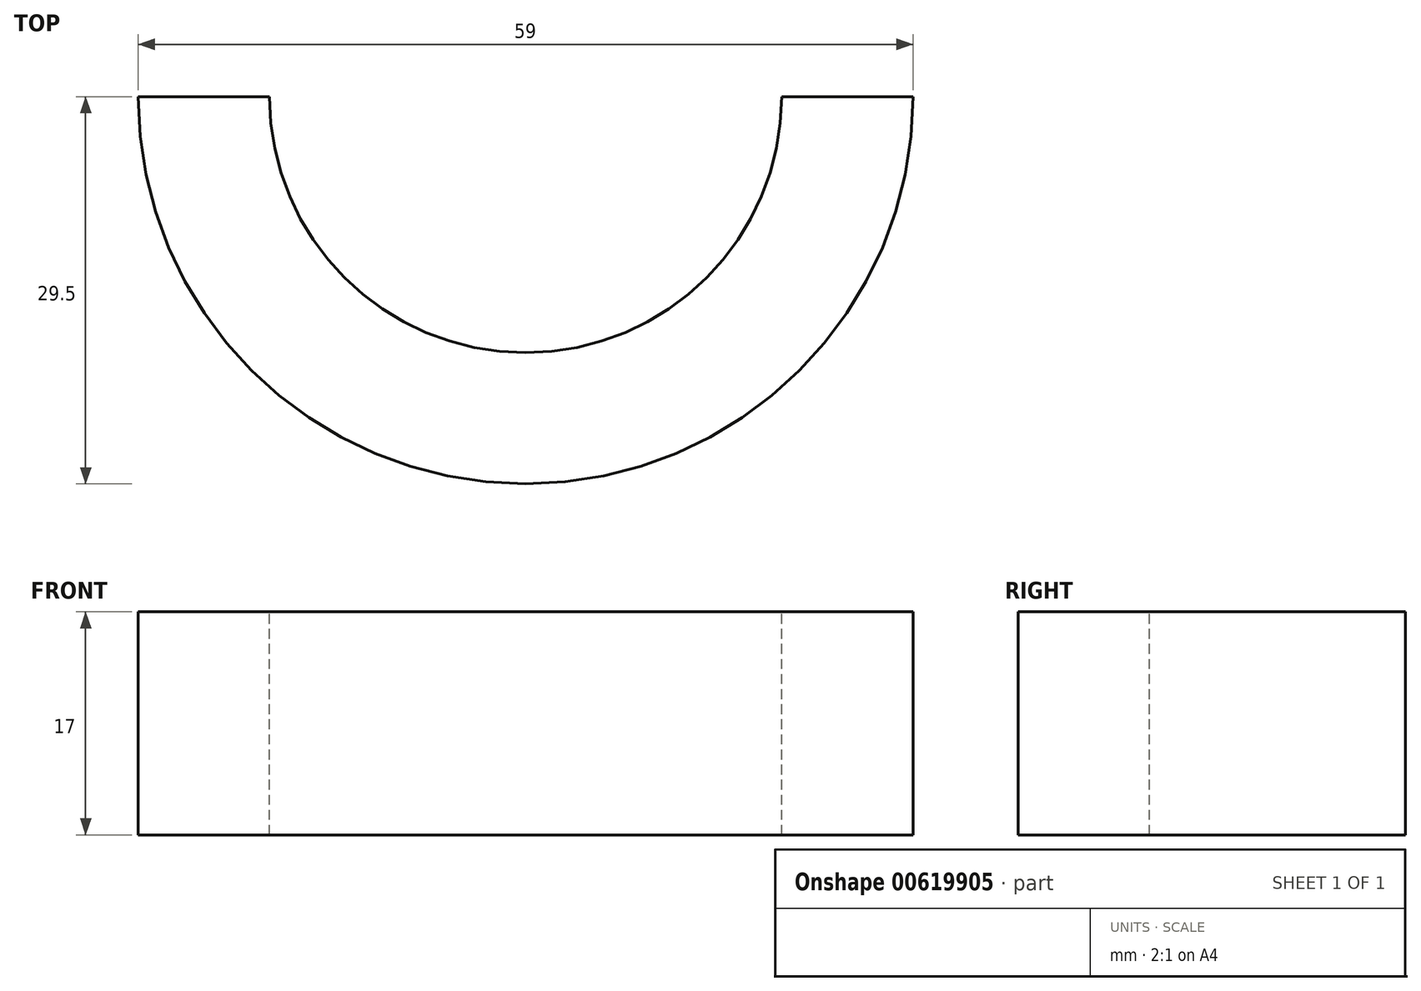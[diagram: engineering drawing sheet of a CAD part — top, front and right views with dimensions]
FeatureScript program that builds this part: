
annotation { "Feature Type Name" : "Feature", "Feature Type Description" : "" }
export const myFeature = defineFeature(function(context is Context, id is Id, definition is map)
    precondition{}
    {
        {
            var Q0;
            Q0=qCreatedBy(makeId("Top.planeOp"),FACE);
            var sketch = newSketch(context, id + "F0", { "sketchPlane" : qUnion([Q0])});
            skCircle(sketch, "E0", {"center": v(0, 0) * mm, "radius": 29.5 * mm});
            skCircle(sketch, "E1", {"center": v(0, 0) * mm, "radius": 19.5 * mm});
            skLineSegment(sketch, "E2", {"start": v(29.5, 0) * mm, "end": v(-29.5, 0) * mm});
            skSolve(sketch);
        }
        {
            var Q0;
            {var subQ0=sQuery(id+"F0.wireOp",EDGE,"E2");var subQ1=sQuery(id+"F0.wireOp",EDGE,"E0");var subQ2=makeQuery(id+"F0.imprint","INTERSECT",VERTEX,{"disambiguationData":[OD(0.0)],"derivedFrom":[subQ1,subQ0]});Q0=makeQuery(id+"F0.imprint","IMPRINT",FACE,{"disambiguationData":[TD([[makeQuery(id+"F0.imprint","IMPRINT",EDGE,{"disambiguationData":[TD([[subQ2,-1.0]])],"derivedFrom":subQ1}),1.0]])]});}
            extrude(context, id + "F1", {"entities" : qUnion([Q0]), "depth" : -17 * mm, "offsetDistance" : 25.4 * mm});
        }
    });
